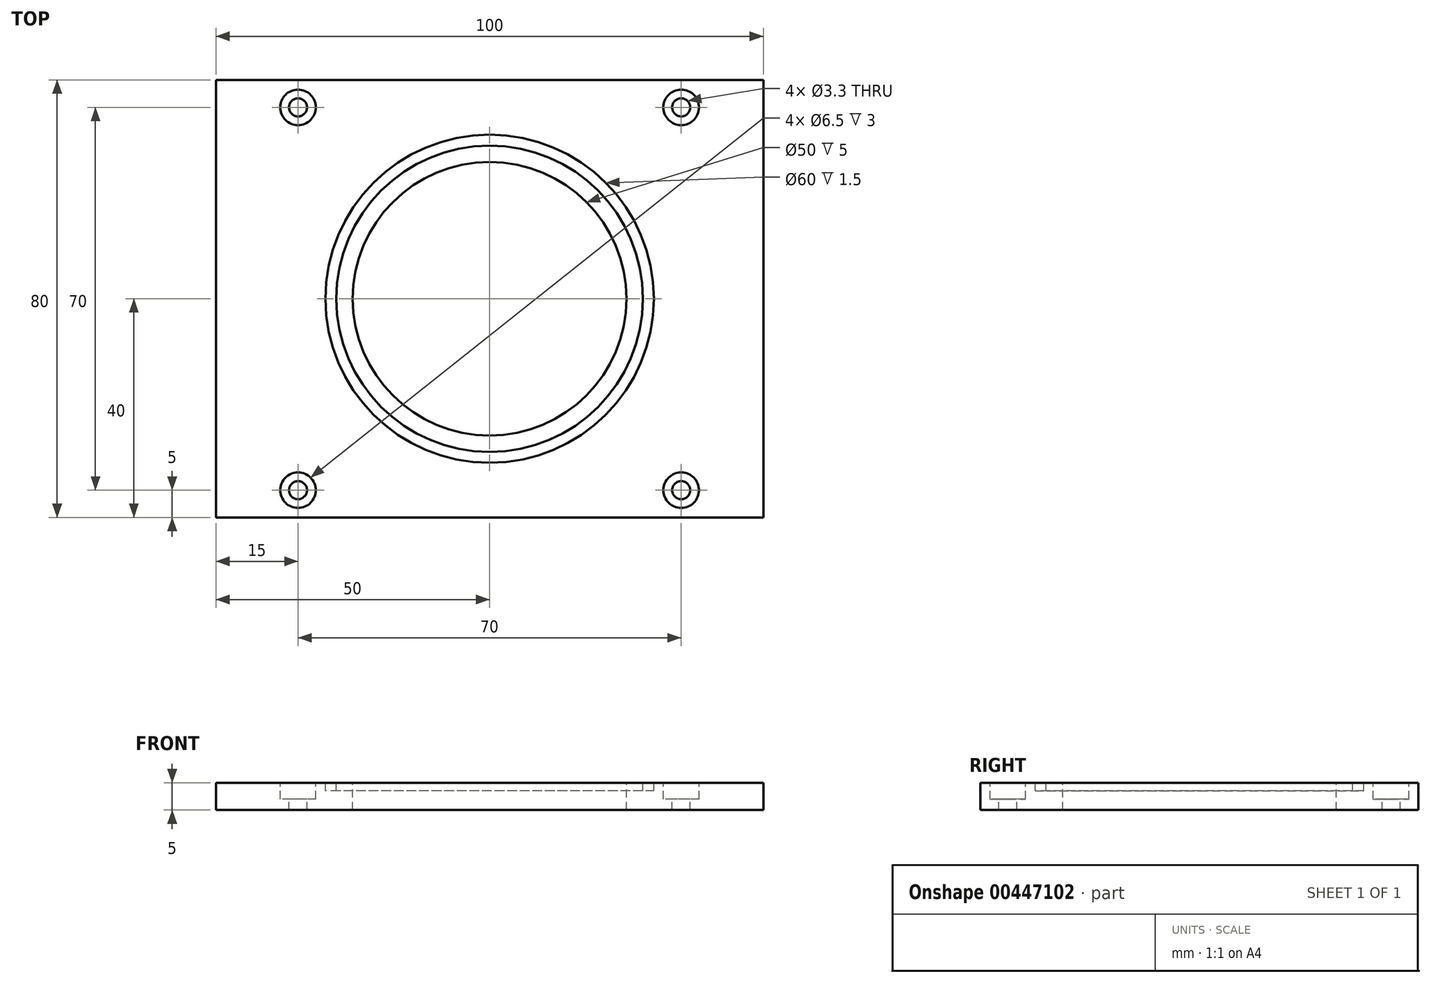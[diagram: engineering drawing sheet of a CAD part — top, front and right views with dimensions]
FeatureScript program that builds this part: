
annotation { "Feature Type Name" : "Feature", "Feature Type Description" : "" }
export const myFeature = defineFeature(function(context is Context, id is Id, definition is map)
    precondition{}
    {
        {
            var Q0;
            Q0=qCreatedBy(makeId("Top.planeOp"),FACE);
            var sketch = newSketch(context, id + "F0", { "sketchPlane" : qUnion([Q0])});
            skLineSegment(sketch, "E0.bottom", {"start": v(50, -40) * mm, "end": v(-50, -40) * mm});
            skLineSegment(sketch, "E0.top", {"start": v(50, 40) * mm, "end": v(-50, 40) * mm});
            skLineSegment(sketch, "E0.left", {"start": v(50, -40) * mm, "end": v(50, 40) * mm});
            skLineSegment(sketch, "E0.right", {"start": v(-50, -40) * mm, "end": v(-50, 40) * mm});
            skPoint(sketch, "E0.middle", {"position": v(0, 0) * mm});
            skSolve(sketch);
        }
        {
            var Q0;
            Q0 = qSketchRegion(id + "F0", true);
            extrude(context, id + "F1", {"entities" : qUnion([Q0]), "endBound" : BoundingType.SYMMETRIC, "depth" : 5 * mm});
        }
        {
            var Q0;
            Q0=makeQuery(id+"F1.opExtrude","CAP_FACE",FACE,{"disambiguationData":[OSD([sQuery(id+"F0.wireOp",EDGE,"E0.bottom"),sQuery(id+"F0.wireOp",EDGE,"E0.top"),sQuery(id+"F0.wireOp",EDGE,"E0.left"),sQuery(id+"F0.wireOp",EDGE,"E0.right")])],"isStart":false});
            var sketch = newSketch(context, id + "F2", { "sketchPlane" : qUnion([Q0])});
            skCircle(sketch, "E1", {"center": v(0, 0) * mm, "radius": 25 * mm});
            skSolve(sketch);
        }
        {
            var Q0;
            Q0 = qSketchRegion(id + "F2", true);
            var Q1;
            Q1=makeQuery(id+"F1.opExtrude","CAP_FACE",FACE,{"disambiguationData":[OSD([sQuery(id+"F0.wireOp",EDGE,"E0.bottom"),sQuery(id+"F0.wireOp",EDGE,"E0.top"),sQuery(id+"F0.wireOp",EDGE,"E0.left"),sQuery(id+"F0.wireOp",EDGE,"E0.right")])],"isStart":true});
            extrude(context, id + "F3", {"entities" : qUnion([Q0]), "operationType" : NewBodyOperationType.REMOVE, "endBound" : BoundingType.UP_TO_SURFACE, "oppositeDirection" : true, "endBoundEntityFace" : qUnion([Q1]), "depth" : 25 * mm});
        }
        {
            var Q0;
            Q0=makeQuery(id+"F1.opExtrude","CAP_FACE",FACE,{"disambiguationData":[OSD([sQuery(id+"F0.wireOp",EDGE,"E0.bottom"),sQuery(id+"F0.wireOp",EDGE,"E0.top"),sQuery(id+"F0.wireOp",EDGE,"E0.left"),sQuery(id+"F0.wireOp",EDGE,"E0.right")])],"isStart":false});
            var sketch = newSketch(context, id + "F4", { "sketchPlane" : qUnion([Q0])});
            skCircle(sketch, "E2", {"center": v(0, 0) * mm, "radius": 28 * mm});
            skCircle(sketch, "E3", {"center": v(0, 0) * mm, "radius": 30 * mm});
            skSolve(sketch);
        }
        {
            var Q0;
            Q0 = qSketchRegion(id + "F4", true);
            extrude(context, id + "F5", {"entities" : qUnion([Q0]), "operationType" : NewBodyOperationType.REMOVE, "oppositeDirection" : true, "depth" : 1.5 * mm});
        }
        {
            var Q0;
            {var subQ0=sQuery(id+"F0.wireOp",EDGE,"E0.left");var subQ1=sQuery(id+"F0.wireOp",EDGE,"E0.top");var subQ2=sQuery(id+"F0.wireOp",EDGE,"E0.right");var subQ3=sQuery(id+"F0.wireOp",EDGE,"E0.bottom");Q0=makeQuery(id+"F5.boolean.opBoolean","SPLIT",FACE,{"disambiguationData":[TD([makeQuery(id+"F1.opExtrude","SWEPT_FACE",FACE,{"disambiguationData":[OSD([subQ3])]})])],"derivedFrom":makeQuery(id+"F1.opExtrude","CAP_FACE",FACE,{"disambiguationData":[OSD([subQ3,subQ1,subQ0,subQ2])],"isStart":false})});}
            var sketch = newSketch(context, id + "F6", { "sketchPlane" : qUnion([Q0])});
            skPoint(sketch, "E4", {"position": v(-35, 35) * mm});
            skPoint(sketch, "E5", {"position": v(35, 35) * mm});
            skPoint(sketch, "E6", {"position": v(-35, -35) * mm});
            skPoint(sketch, "E7", {"position": v(35, -35) * mm});
            skSolve(sketch);
        }
        {
            var Q0;
            Q0=sQuery(id+"F6.wireOp",VERTEX,"E4");
            var Q1;
            Q1=sQuery(id+"F6.wireOp",VERTEX,"E5");
            var Q2;
            Q2=sQuery(id+"F6.wireOp",VERTEX,"E7");
            var Q3;
            Q3=sQuery(id+"F6.wireOp",VERTEX,"E6");
            var Q4;
            Q4=makeQuery(id+"F1.opExtrude","SWEPT_BODY",BODY,{"disambiguationData":[OSD([sQuery(id+"F0.wireOp",EDGE,"E0.bottom"),sQuery(id+"F0.wireOp",EDGE,"E0.top"),sQuery(id+"F0.wireOp",EDGE,"E0.left"),sQuery(id+"F0.wireOp",EDGE,"E0.right")])]});
            hole(context, id + "F7", {"style" : HoleStyle.C_BORE, "endStyle" : HoleEndStyle.THROUGH, "standardTappedOrClearance" : lookupTablePath({ "standard" : "ISO", "fit" : "Normal", "size" : "M3", "type" : "Clearance" }), "standardBlindInLast" : lookupTablePath({ "fit" : "Standard", "standard" : "ISO", "size" : "M3", "type" : "Clearance" }), "holeDiameter" : 3.3 * mm, "cBoreDiameter" : 6.5 * mm, "cBoreDepth" : 3 * mm, "isTappedThrough" : true, "tappedDepth" : 12 * mm, "tapClearance" : 3, "locations" : qUnion([Q0, Q1, Q2, Q3]), "scope" : qUnion([Q4])});
        }
    });
